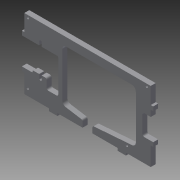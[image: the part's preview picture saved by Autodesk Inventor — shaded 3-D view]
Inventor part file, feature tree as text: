
AUTODESK INVENTOR PART (.ipt)
format: ipt  version: 2015 (Build 190159000, 159)  size: 260,608 bytes
history: native  units: mm
features: extrude x5, sketch x5, fillet x5
ambient origin geometry x8: Origin, YZ Plane, XZ Plane, XY Plane, X Axis, Y Axis, Z Axis, Center Point
bodies: Solid1 (feature_tree)
feature tree (15):
  extrude  "Extrusion1"  Depth=153.0mm
  extrude  "Extrusion2"  Depth=20.0mm
  sketch  "Sketch3"  dims[d5=5.0mm d6=3.0mm d7=12.5mm d9=3.0mm]
  extrude  "Extrusion5"  Depth=3.0mm
  fillet  "Fillet2"  Radius=12.5mm
  fillet  "Fillet3"  Radius=3.0mm
  extrude  "Extrusion6"  Depth=3.0mm
  extrude  "Extrusion8"  Depth=20.0mm
  fillet  "Fillet8"  Radius=6.0mm
  fillet  "Fillet9"  Radius=20.0mm
  fillet  "Fillet10"  Radius=42.0mm
  sketch  "Sketch1"  dims[d0=85.0mm d1=153.0mm]
  sketch  "Sketch2"  dims[d3=3.0mm d4=20.0mm]
  sketch  "Sketch6"  dims[d10=5.0mm d11=3.0mm]
  sketch  "Sketch7"  dims[d12=12.5mm d13=20.0mm d14=6.0mm d15=0.0mm d16=20.0mm d22=42.0mm d24=3.0mm d26=6.0mm d28=20.0mm d30=6.0mm d31=0.0mm d33=6.0mm d34=10.0mm d35=18.0mm d39=10.0mm d40=3.0mm d41=10.0mm d42=3.0mm d43=30.0mm d44=30.0mm d47=2.0mm d66=5.0mm d67=5.0mm d69=20.0mm d71=12.5mm d72=10.0mm d73=20.0mm d74=6.0mm d75=25.0mm d77=20.0mm d78=10.0mm d79=10.0mm d80=0.0mm d81=2.0mm d82=1.0mm d84=3.0mm d86=4.0mm d87=3.0mm d88=3.0mm d89=74.0mm d90=3.0mm d91=144.0mm d92=3.0mm d93=24.0mm d94=10.0mm d95=0.0mm d96=42.0mm d97=10.0mm d106=10.0mm d107=89.0mm d114=12.0mm d115=30.5mm d116=12.0mm d118=10.0mm d119=0.0mm d120=1.0mm d121=0.5mm d122=41.0mm d123=6.0mm d127=8.0mm d128=8.0mm d129=2.0mm]
